# Revit family: Cascade-Systems_Quinta Pro_5-Boilers_Air-Dirt-Separator_Wall-Mount_v2011
name_source: partatom
category: Mechanical Equipment
revit_build: Autodesk Revit MEP 2012 (Build: 20110309_2315(x64)
units: mm (PartAtom-declared; Revit-internal decimal feet)

## types (5) — shared parameters
Air Supply Pipe Radius = 80.000 mm
Apparent Load = 0 VA
Assembly Code = D3020100
Back Clearance = 0.000 mm
Between Boilers Clearance = 30.000 mm
Boiler Unit = Metal - Reflective - White
Clearence Box = Glass - Clear - Amber
Combustion Gas Exhaust Pipe Radius = 40.000 mm
Connection Note = If primary connections to low loss header is to the front or rear of the cascade system please view Cascade technical manual for further dimensional clearances.
Controls Voltage = 24 (max 4va)
DN100 Primary 461 - 642kW_Gas Connection_DIN 2633 - 4 hole = DN65
DN100 Primary 461 - 642kW_Primary Flow Connection to Header_PN6 DIN2631-  4 Hole = DN100
DN100 Primary 461 - 642kW_Primary Return Connection to Header_PN6 DIN2631-  4 Hole = DN100
DN100 Primary 461 - 642kW_Secondary Flow Connection to Header_PN6 DIN2631-  4 Hole = DN125
DN100 Primary 461 - 642kW_Secondary Return Connection to Header_PN6 DIN2631-  4 Hole = DN125
DN65 Primary 0 - 460kW_Gas Connection_DIN 2633 - 4 hole = DN50
DN65 Primary 0 - 460kW_Primary Flow Connection to Header_PN6 DIN2631-  4 HolePN6 DIN2631-  4 Hole = DN65
DN65 Primary 0 - 460kW_Primary Return Connection to Header_PN6 DIN2631-  4 HolePN6 DIN2631-  4 Hole = DN65
DN65 Primary 0 - 460kW_Secondary Flow Connection to Header_PN6 DIN2631-  4 Hole = DN100
DN65 Primary 0 - 460kW_Secondary Return Connection to Header_PN6 DIN2631-  4 Hole = DN100
Default Elevation = 0.000 mm
Description = Condensing Boiler
Expansions Vessel Connection = Yes
Filling Valve / Drain Valve = Yes
Flame Protection = Ionisation
Flow Connection Diameter - 35 x 1,5 to Main Pipe = 35.000 mm
Flow Connection Isolating Valve = Yes
Flow Pipe = Paint - Red
Front Clearance = 1000.000 mm
Fuse Rating = 6 A
Gas Connection BSP = 19.050 mm
Gas Connection Isolating Valve = Yes
Gas Connection Pipe Diameter = 19.050 mm
Gas Connection Pipe Radius = 9.525 mm
Gas Pipe = Paint - Yellow
Heating Circuit Flow Diameter = 31.750 mm
Heating Circuit Flow Pipe Radius = 15.875 mm
Heating Circuit Return Pipe Diameter = 31.750 mm
Heating Circuit Return Pipe Radius = 15.875 mm
High limit set point  deg C = 110 deg C
Host Condition = Wall Hung
Hydraulic-Deaerator_Dirt-Separator = Metal - Brass - Polished
Ignition = Electronic
Installation URL = http://www.remeha.co.uk
Instrument Box Panel = Metal - Polished Silver
Insulation = Insulation - Black
Insulation Class IP = X4D
Insulation Visibility = Yes
Isolating Valve = Yes
Load Classification = Power
Load Sub-Classification Motor = Yes
Low Loss Header Clearance = 650.000 mm
Low Loss Header Clearance DN100 = 650.000 mm
Low Loss Header Clearance DN65 = 650.000 mm
Manufacturer = Remeha Commercial
Manufacturer Fax = 0118 978 6977
Maximum operating pressure  bar = 4 bar
Min / Max gas pressure mbar LPG = 37 - 50 mbar
Min / Max gas pressures mbar NG = 17 - 30 mbar
Minimum flow rate m3/hr (water flow) = 0.4 m3/hr
Minimum operating pressure  bar = 0.8 bar
Modulating Input V dc = 0 -10
No Of Boilers = 5
Non Return Valve = Yes
Note = Primary pipework set and low loss header dependant on kW rating of the cascade systerm. Use DN65 on 0 - 460kW systems and Use DN100 on 461 - 642kW
Number of Poles = 1
Optional Fuel = Propane
Power Factor = 1
Power Supply = 230v – 1ph – 50hz
Product Page URL = http://www.remeha.co.uk
Return Connection Diameter - 35 x 1,5 to Main Pipe = 35.000 mm
Return Pipe = Paint - Blue
Safety Valve = Yes
Sales Brochure = http://www.remeha.co.uk
Siphon Bush Pipe Diameter = 19.000 mm
Siphon Bush Pipe Radius = 9.500 mm
Standard Fuel Available = Natural Gas
Standard Operating Temperature = 20 – 90 deg C
Start Current = 2 A
Subcategory = Condensing Boilers
Technical Information URL = http://www.remeha.co.uk
Text Material = Paint - Black
Top Clearance = 400.000 mm
URL = http://www.remeha.co.uk
Voltage = 230 V

## per-type parameters (varying)
| type | Concentric Connection | Efficiency Full load @ 80 / 60 c NCV % | Flue Gas temperature deg C | Fuel consumption m3 /hr LPG | Fuel consumption m3/hr Natural Gas | Low Loss Header_DN 100 | Low Loss Header_DN 65 | Maximum flue gas flow rate Kg/hr | Model | NOx mg/kW dry | Noise levels dB(A) at 1 metre | Nominal flow rate @ 11 dT l/s | Nominal flow rate @ 20 dT l/s | OV | Power Consumption Full Load W | Power Consumption Part Load W | Power Consumption Standby   W | Radiated losses @ 30 deg C | Rated output kW 50 / 30 | Rated output kW 80 / 60 | Resistance @11 deg dT | Resistance at 20 deg dT | Water Content | Weight Kg |
| Wall-Mounted_5-Boiler_Quinta Pro 30 | 80 – 125mm | 97.50% | 65 deg c | 1.3 m3/h | 3.3 m3/h | No | Yes | 50 Kg/h | Quinta Pro 30 | 37 Mg/kWh | 38 dB(A) | 0.64 l/s | 0.35 l/s | 569.000 mm | 39 | 18 | 5 | 0.303 | 31.4 kW | 29.3 kW | 231 mbar | 70 mbar | 5.50 L | 53 kgf |
| Wall-Mounted_5-Boiler_Quinta Pro 45 | 80 – 125mm | 97.20% | 67 deg C | 1.7 m3/h | 4.4 m3/h | No | Yes | 69 Kg/h | Quinta Pro 45 | 37 Mg/kWh | 45 dB(A) | 0.87 l/s | 0.48 l/s | 569.000 mm | 68 | 18 | 5 | 0.245 | 43 kW | 40 kW | 297 mbar | 90 mbar | 5.50 L | 53 kgf |
| Wall-Mounted_5-Boiler_Quinta Pro 65 | 100 – 150mm | 98.30% | 68 deg C | 2.5 m3/h | 6.6 m3/h | No | Yes | 104 Kg/h | Quinta Pro 65 | 32 Mg/kWh | 45 dB(A) | 1.33 l/s | 0.77 l/s | 569.000 mm | 88 | 23 | 6 | 0.177 | 65 kW | 61 kW | 430 mbar | 130 mbar | 6.50 L | 60 kgf |
| Wall-Mounted_5-Boiler_Quinta Pro 90 | 100 – 150mm | 97.90% | 68 deg C | 3.5 m3/h | 9.1 m3/h | No | Yes | 138 Kg/h | Quinta Pro 90 | 29 Mg/kWh | 52 dB(A) | 1.83 l/s | 1.00 l/s | 569.000 mm | 125 | 20 | 4 | 0.143 | 89.5 kW | 84.2 kW | 463 mbar | 140 mbar | 7.50 L | 67 kgf |
| Wall-Mounted_5-Boiler_Quinta Pro 115 | 100 – 150mm | 96.60% | 72 deg c | 4.7 m3/h | 11.7 m3/h | Yes | No | 178 Kg/h | Quinta Pro 115 | 35 Mg/kWh | 51 dB(A) | 2.22 l/s | 1.28 l/s | 875.000 mm | 199 | 45 | 7 | 0.112 | 114 kW | 107 kW | 826 mbar | 250 mbar | 7.50 L | 68 kgf |

## geometry (parser evidence)
native form markers: Blend x20, Sweep x17
no freeform markers — native parametric forms only
